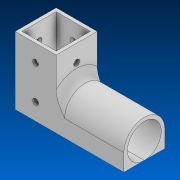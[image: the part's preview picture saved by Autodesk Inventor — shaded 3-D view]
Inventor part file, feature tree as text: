
AUTODESK INVENTOR PART (.ipt)
format: ipt  version: 2022.2 (Build 262287000, 287)  size: 148,992 bytes
history: native  units: in
note: dims shown in document units (in); Inventor stores cm internally (conversion verified against a paired STEP export)
features: sketch x4, extrude x3, hole x2, fillet x1
ambient origin geometry x8: Origin, YZ Plane, XZ Plane, XY Plane, X Axis, Y Axis, Z Axis, Center Point
bodies: Solid1 (feature_tree)
feature tree (10):
  extrude  "Extrusion1"  Depth=1.01in
  hole  "Hole1"  [1 undecoded]
  hole  "Hole2"  [1 undecoded]
  sketch  "Sketch4"  dims[d7=0.175in d8=0.75in d9=0.375in d10=0.25in d11=0.5635in d12=1.0in d13=0.8108in d14=0.175in d15=0.75in d16=0.375in d17=0.25in d18=0.5635in d19=1.0in d20=0.8108in d21=2.0in d22=0.0in d23=2.0in d24=0.0in d25=0.25in]
  extrude  "Extrusion2"  Depth=0.25in TaperAngle=0.0deg
  extrude  "Extrusion3"  Depth=0.25in TaperAngle=0.0deg
  fillet  "Fillet1"  Radius=0.25in
  sketch  "Sketch1"  dims[d0=1.01in d1=1.01in]
  sketch  "Sketch2"  dims[d2=0.1in d3=2.0in d4=0.0in]
  sketch  "Sketch3"  dims[d5=0.5in d6=1.0in]
note: 2 required parameter values undecoded (feature->parameter linkage not recoverable at this tier; creation-order binding heuristic only, values carry confidence <= 0.55)
